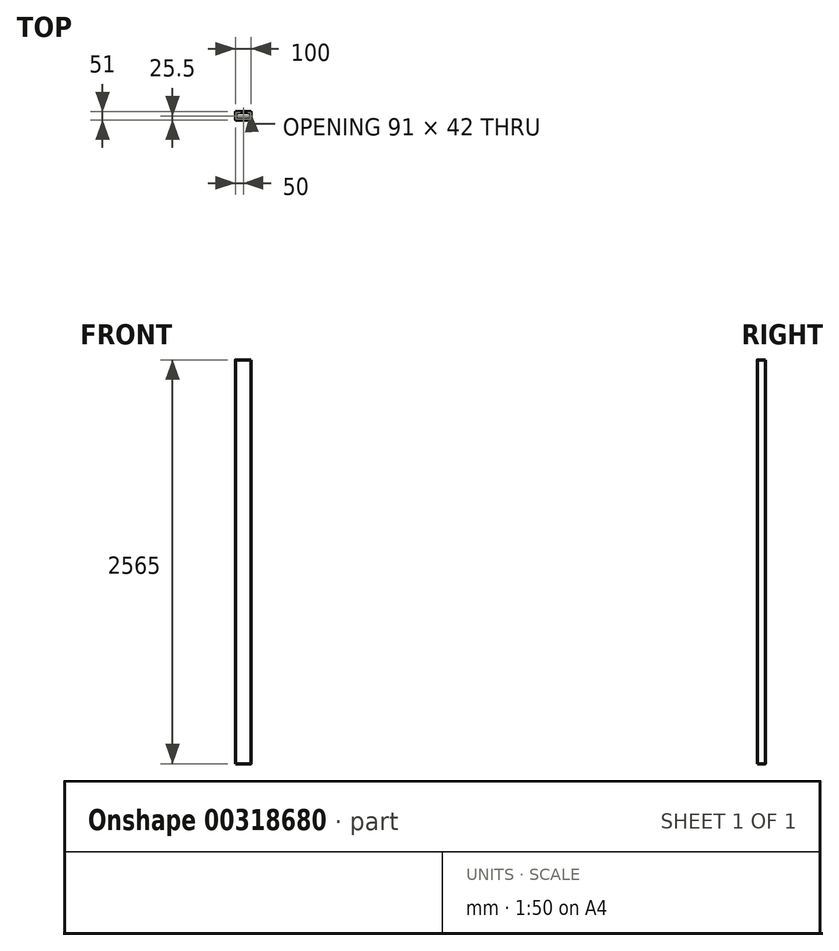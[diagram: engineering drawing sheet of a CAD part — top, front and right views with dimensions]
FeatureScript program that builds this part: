
annotation { "Feature Type Name" : "Feature", "Feature Type Description" : "" }
export const myFeature = defineFeature(function(context is Context, id is Id, definition is map)
    precondition{}
    {
        {
            var Q0;
            Q0=qCreatedBy(makeId("Top.planeOp"),FACE);
            var sketch = newSketch(context, id + "F0", { "sketchPlane" : qUnion([Q0])});
            skLineSegment(sketch, "E0.bottom", {"start": v(48, -25.5) * mm, "end": v(-48, -25.5) * mm});
            skLineSegment(sketch, "E0.top", {"start": v(48, 25.5) * mm, "end": v(-48, 25.5) * mm});
            skLineSegment(sketch, "E0.left", {"start": v(50, -23.5) * mm, "end": v(50, 23.5) * mm});
            skLineSegment(sketch, "E0.right", {"start": v(-50, -23.5) * mm, "end": v(-50, 23.5) * mm});
            skPoint(sketch, "E0.middle", {"position": v(0, 0) * mm});
            skPoint(sketch, "E1.visualSharp", {"position": v(-50, 25.5) * mm});
            skArc(sketch, "E1.filletArc", {"start": v(-48, 25.5) * mm, "mid": v(-49.41, 24.91) * mm, "end": v(-50, 23.5) * mm});
            skPoint(sketch, "E2.visualSharp", {"position": v(50, 25.5) * mm});
            skArc(sketch, "E2.filletArc", {"start": v(50, 23.5) * mm, "mid": v(49.41, 24.91) * mm, "end": v(48, 25.5) * mm});
            skPoint(sketch, "E3.visualSharp", {"position": v(50, -25.5) * mm});
            skArc(sketch, "E3.filletArc", {"start": v(48, -25.5) * mm, "mid": v(49.41, -24.91) * mm, "end": v(50, -23.5) * mm});
            skPoint(sketch, "E4.visualSharp", {"position": v(-50, -25.5) * mm});
            skArc(sketch, "E4.filletArc", {"start": v(-50, -23.5) * mm, "mid": v(-49.41, -24.91) * mm, "end": v(-48, -25.5) * mm});
            skLineSegment(sketch, "E5.0", {"start": v(43.5, 21) * mm, "end": v(-43.5, 21) * mm});
            skLineSegment(sketch, "E6.0", {"start": v(43.5, -21) * mm, "end": v(-43.5, -21) * mm});
            skLineSegment(sketch, "E7.0", {"start": v(45.5, -19) * mm, "end": v(45.5, 19) * mm});
            skLineSegment(sketch, "E8.0", {"start": v(-45.5, -19) * mm, "end": v(-45.5, 19) * mm});
            skArc(sketch, "E9.filletArc", {"start": v(45.5, 19) * mm, "mid": v(44.91, 20.41) * mm, "end": v(43.5, 21) * mm});
            skArc(sketch, "E10.filletArc", {"start": v(43.5, -21) * mm, "mid": v(44.91, -20.41) * mm, "end": v(45.5, -19) * mm});
            skArc(sketch, "E11.filletArc", {"start": v(-45.5, -19) * mm, "mid": v(-44.91, -20.41) * mm, "end": v(-43.5, -21) * mm});
            skArc(sketch, "E12.filletArc", {"start": v(-43.5, 21) * mm, "mid": v(-44.91, 20.41) * mm, "end": v(-45.5, 19) * mm});
            skSolve(sketch);
        }
        {
            var Q0;
            Q0=makeQuery(id+"F0.imprint","IMPRINT",FACE,{"disambiguationData":[TD([[makeQuery(id+"F0.imprint","IMPRINT",EDGE,{"derivedFrom":sQuery(id+"F0.wireOp",EDGE,"E0.bottom")}),-1.0]])]});
            extrude(context, id + "F1", {"entities" : qUnion([Q0]), "depth" : 2565 * mm});
        }
    });
